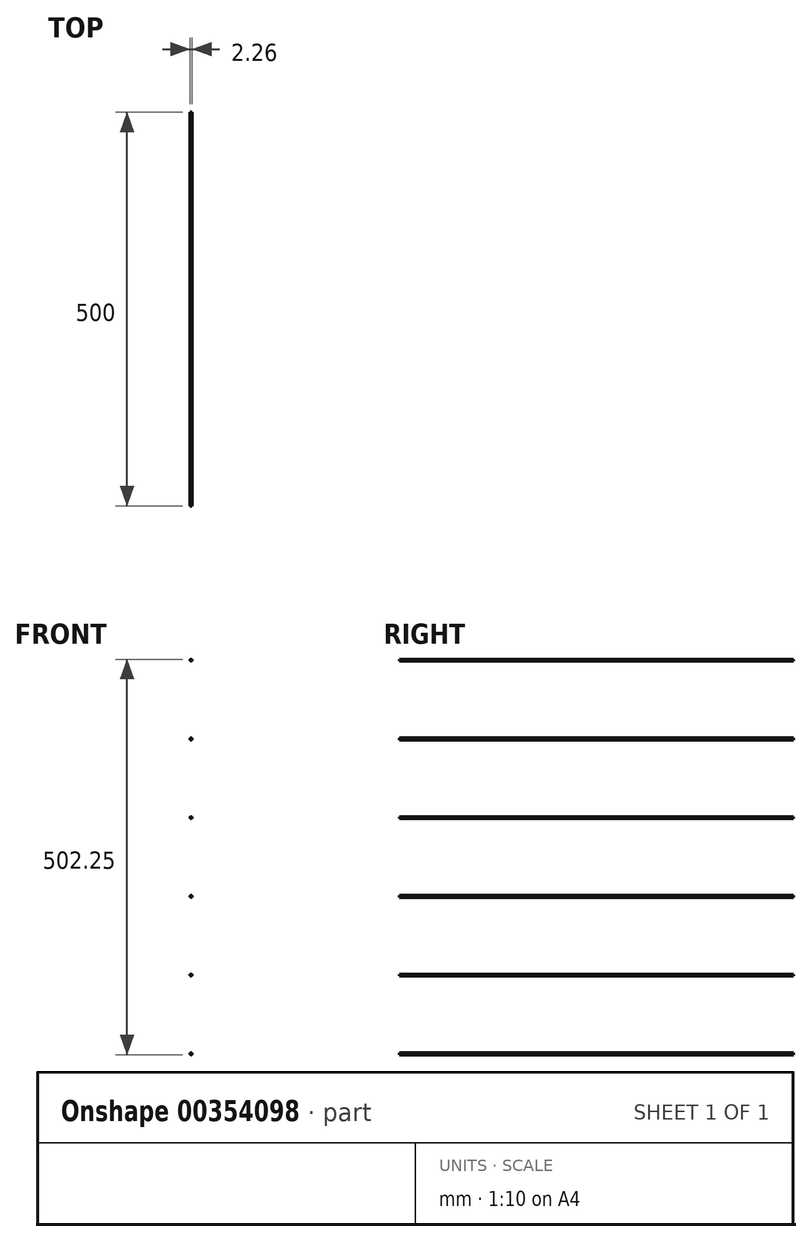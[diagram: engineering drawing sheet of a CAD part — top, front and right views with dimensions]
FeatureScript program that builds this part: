
annotation { "Feature Type Name" : "Feature", "Feature Type Description" : "" }
export const myFeature = defineFeature(function(context is Context, id is Id, definition is map)
    precondition{}
    {
        {
            var Q0;
            Q0=qCreatedBy(makeId("Right.planeOp"),FACE);
            var sketch = newSketch(context, id + "F0", { "sketchPlane" : qUnion([Q0])});
            skLineSegment(sketch, "E0", {"start": v(-1030.18, 276.22) * mm, "end": v(-530.18, 276.22) * mm});
            skLineSegment(sketch, "E1", {"start": v(-1030.18, 176.22) * mm, "end": v(-530.18, 176.22) * mm});
            skLineSegment(sketch, "E2", {"start": v(-1030.18, 76.22) * mm, "end": v(-530.18, 76.22) * mm});
            skLineSegment(sketch, "E3", {"start": v(-1030.18, -23.78) * mm, "end": v(-530.18, -23.78) * mm});
            skLineSegment(sketch, "E4", {"start": v(-1030.18, -123.78) * mm, "end": v(-530.18, -123.78) * mm});
            skLineSegment(sketch, "E5", {"start": v(-1030.18, -223.78) * mm, "end": v(-530.18, -223.78) * mm});
            skLineSegment(sketch, "E6", {"start": v(-1030.18, 276.22) * mm, "end": v(-1030.18, -409.58) * mm, "construction": true});
            skLineSegment(sketch, "E7", {"start": v(-530.18, 276.22) * mm, "end": v(-530.18, -486.49) * mm, "construction": true});
            skSolve(sketch);
        }
        {
            var Q0;
            Q0=qCreatedBy(makeId("Front.planeOp"),FACE);
            var Q1;
            Q1=sQuery(id+"F0.wireOp",VERTEX,"E7.start");
            cPlane(context, id + "F1", {"entities" : qUnion([Q0, Q1]), "cplaneType" : CPlaneType.PLANE_POINT, "offset" : 25 * mm, "width" : 150 * mm, "height" : 150 * mm});
        }
        {
            var Q0;
            Q0=qCreatedBy(id+"F1.planeOp",FACE);
            var sketch = newSketch(context, id + "F2", { "sketchPlane" : qUnion([Q0])});
            skCircle(sketch, "E8", {"center": v(0, 276.22) * mm, "radius": 1.13 * mm});
            skCircle(sketch, "E9", {"center": v(0, 176.22) * mm, "radius": 1.13 * mm});
            skCircle(sketch, "E10", {"center": v(0, 76.22) * mm, "radius": 1.13 * mm});
            skCircle(sketch, "E11", {"center": v(0, -23.78) * mm, "radius": 1.13 * mm});
            skCircle(sketch, "E12", {"center": v(0, -123.78) * mm, "radius": 1.13 * mm});
            skCircle(sketch, "E13", {"center": v(0, -223.78) * mm, "radius": 1.13 * mm});
            skSolve(sketch);
        }
        {
            var Q0;
            Q0=makeQuery(id+"F2.imprint","IMPRINT",FACE,{"disambiguationData":[TD([[makeQuery(id+"F2.imprint","IMPRINT",EDGE,{"derivedFrom":sQuery(id+"F2.wireOp",EDGE,"E10")}),1.0]])]});
            var Q1;
            Q1=sQuery(id+"F0.wireOp",EDGE,"E2");
            sweep(context, id + "F3", {"profiles" : qUnion([Q0]), "path" : qUnion([Q1])});
        }
        {
            var Q0;
            Q0 = qSketchRegion(id + "F2", true);
            var Q1;
            Q1=sQuery(id+"F0.wireOp",EDGE,"E0");
            sweep(context, id + "F4", {"operationType" : NewBodyOperationType.ADD, "profiles" : qUnion([Q0]), "path" : qUnion([Q1])});
        }
    });
